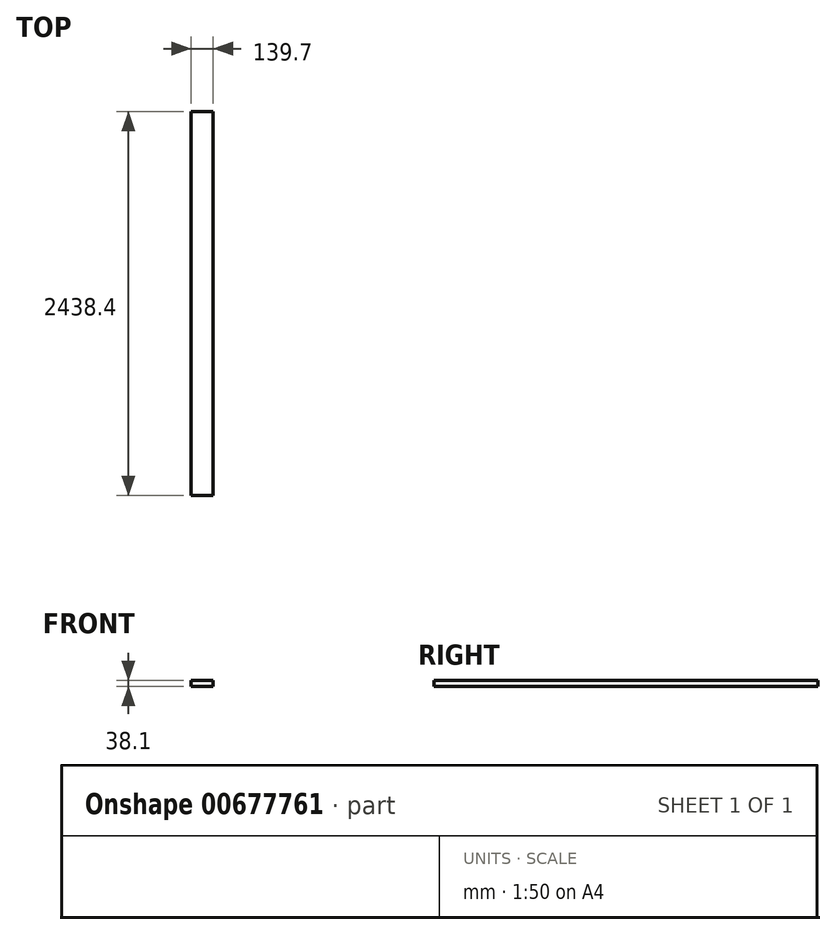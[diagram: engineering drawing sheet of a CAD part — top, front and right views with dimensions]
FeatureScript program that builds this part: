
annotation { "Feature Type Name" : "Feature", "Feature Type Description" : "" }
export const myFeature = defineFeature(function(context is Context, id is Id, definition is map)
    precondition{}
    {
        {
            var Q0;
            Q0=qCreatedBy(makeId("Front.planeOp"),FACE);
            var sketch = newSketch(context, id + "F0", { "sketchPlane" : qUnion([Q0])});
            skLineSegment(sketch, "E0.bottom", {"start": v(-931.07, -59.15) * mm, "end": v(-1070.77, -59.15) * mm});
            skLineSegment(sketch, "E0.top", {"start": v(-931.07, -97.25) * mm, "end": v(-1070.77, -97.25) * mm});
            skLineSegment(sketch, "E0.left", {"start": v(-931.07, -59.15) * mm, "end": v(-931.07, -97.25) * mm});
            skLineSegment(sketch, "E0.right", {"start": v(-1070.77, -59.15) * mm, "end": v(-1070.77, -97.25) * mm});
            skSolve(sketch);
        }
        {
            var Q0;
            Q0=makeQuery(id+"F0.imprint","IMPRINT",FACE,{"disambiguationData":[TD([[makeQuery(id+"F0.imprint","IMPRINT",EDGE,{"derivedFrom":sQuery(id+"F0.wireOp",EDGE,"E0.bottom")}),1.0]])]});
            extrude(context, id + "F1", {"entities" : qUnion([Q0]), "depth" : 2438.4 * mm, "offsetDistance" : 25.4 * mm});
        }
    });
